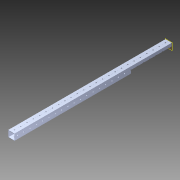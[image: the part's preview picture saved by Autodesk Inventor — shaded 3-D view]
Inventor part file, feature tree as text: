
AUTODESK INVENTOR PART (.ipt)
format: ipt  version: 2014 (Build 180170000, 170)  size: 1,352,192 bytes
history: native  units: in
note: dims shown in document units (in); Inventor stores cm internally (conversion verified against a paired STEP export)
features: extrude x3, sketch x3, reference x2, pattern_circular x1, other x1, plane x1, imported_body x1
ambient origin geometry x8: Origin, YZ Plane, XZ Plane, XY Plane, X Axis, Y Axis, Z Axis, Center Point
bodies: Body1 (feature_tree)
feature tree (12):
  pattern_circular  "CirPattern2"
  other  "217-3426-STEP1"
  plane  "Work Plane1"
  extrude  "Extrusion1"  Depth=3937.0079in TaperAngle=0.0deg
  extrude  "Extrusion3"  Depth=0.5in
  extrude  "Extrusion4"  Depth=0.0787in
  imported_body  "Base1"
  sketch  "Sketch1"  dims[d0=-25.0in d1=3937.0079in d2=0.0in]
  sketch  "Sketch4"  dims[d10=3.937in d11=0.0in d12=0.5in]
  reference  "Reference2"
  reference  "Reference3"
  sketch  "Sketch5"  dims[d13=6.5in d14=0.0787in d15=3.937in d16=0.0in]
